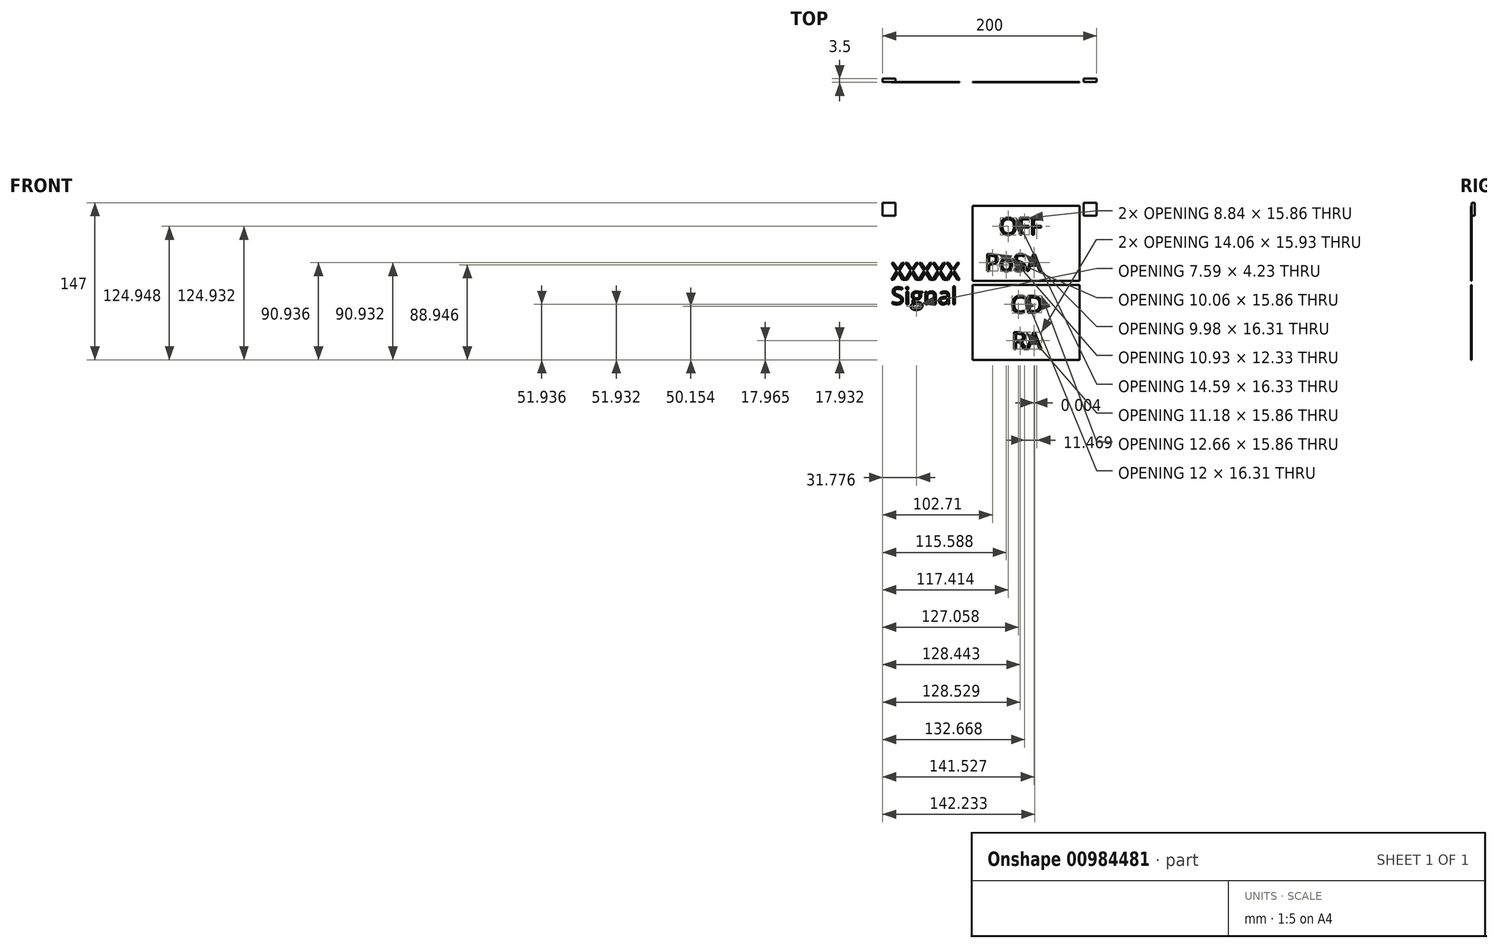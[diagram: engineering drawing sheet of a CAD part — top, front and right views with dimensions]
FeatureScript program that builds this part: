
annotation { "Feature Type Name" : "Feature", "Feature Type Description" : "" }
export const myFeature = defineFeature(function(context is Context, id is Id, definition is map)
    precondition{}
    {
        {
            var Q0;
            Q0=qCreatedBy(makeId("Front.planeOp"),FACE);
            var sketch = newSketch(context, id + "F0", { "sketchPlane" : qUnion([Q0])});
            skLineSegment(sketch, "E0.bottom", {"start": v(-152.92, 118.64) * mm, "end": v(47.08, 118.64) * mm});
            skLineSegment(sketch, "E0.top", {"start": v(-152.92, -31.36) * mm, "end": v(47.08, -31.36) * mm});
            skLineSegment(sketch, "E0.left", {"start": v(-152.92, 118.64) * mm, "end": v(-152.92, -31.36) * mm});
            skLineSegment(sketch, "E0.right", {"start": v(47.08, 118.64) * mm, "end": v(47.08, -31.36) * mm});
            skLineSegment(sketch, "E1.bottom", {"start": v(-140.92, 118.64) * mm, "end": v(-152.92, 118.64) * mm});
            skLineSegment(sketch, "E1.top", {"start": v(-140.92, 106.64) * mm, "end": v(-152.92, 106.64) * mm});
            skLineSegment(sketch, "E1.left", {"start": v(-140.92, 118.64) * mm, "end": v(-140.92, 106.64) * mm});
            skLineSegment(sketch, "E1.right", {"start": v(-152.92, 118.64) * mm, "end": v(-152.92, 106.64) * mm});
            skLineSegment(sketch, "E2.bottom", {"start": v(47.08, 106.64) * mm, "end": v(35.08, 106.64) * mm});
            skLineSegment(sketch, "E2.top", {"start": v(47.08, 118.64) * mm, "end": v(35.08, 118.64) * mm});
            skLineSegment(sketch, "E2.left", {"start": v(47.08, 106.64) * mm, "end": v(47.08, 118.64) * mm});
            skLineSegment(sketch, "E2.right", {"start": v(35.08, 106.64) * mm, "end": v(35.08, 118.64) * mm});
            skLineSegment(sketch, "E3.bottom", {"start": v(47.08, -19.36) * mm, "end": v(35.08, -19.36) * mm});
            skLineSegment(sketch, "E3.top", {"start": v(47.08, -31.36) * mm, "end": v(35.08, -31.36) * mm});
            skLineSegment(sketch, "E3.left", {"start": v(47.08, -19.36) * mm, "end": v(47.08, -31.36) * mm});
            skLineSegment(sketch, "E3.right", {"start": v(35.08, -19.36) * mm, "end": v(35.08, -31.36) * mm});
            skLineSegment(sketch, "E4.bottom", {"start": v(-152.92, -19.36) * mm, "end": v(-140.92, -19.36) * mm});
            skLineSegment(sketch, "E4.top", {"start": v(-152.92, -31.36) * mm, "end": v(-140.92, -31.36) * mm});
            skLineSegment(sketch, "E4.left", {"start": v(-152.92, -19.36) * mm, "end": v(-152.92, -31.36) * mm});
            skLineSegment(sketch, "E4.right", {"start": v(-140.92, -19.36) * mm, "end": v(-140.92, -31.36) * mm});
            skCircle(sketch, "E5", {"center": v(13.08, 96.64) * mm, "radius": 11 * mm});
            skCircle(sketch, "E6", {"center": v(13.08, 62.64) * mm, "radius": 11 * mm});
            skCircle(sketch, "E7", {"center": v(13.08, 23.64) * mm, "radius": 11 * mm});
            skCircle(sketch, "E8", {"center": v(13.08, -10.36) * mm, "radius": 11 * mm});
            skSolve(sketch);
        }
        {
            var Q0;
            Q0=makeQuery(id+"F0.imprint","IMPRINT",FACE,{"disambiguationData":[TD([[makeQuery(id+"F0.imprint","IMPRINT",EDGE,{"derivedFrom":sQuery(id+"F0.wireOp",EDGE,"E0.bottom")}),-1.0]])]});
            extrude(context, id + "F1", {"entities" : qUnion([Q0]), "depth" : 3 * mm, "offsetDistance" : 25 * mm});
        }
        {
            var Q0;
            Q0=makeQuery(id+"F1.opExtrude","CAP_FACE",FACE,{"disambiguationData":[OSD([sQuery(id+"F0.wireOp",EDGE,"E0.bottom"),sQuery(id+"F0.wireOp",EDGE,"E0.top"),sQuery(id+"F0.wireOp",EDGE,"E0.left"),sQuery(id+"F0.wireOp",EDGE,"E0.right"),sQuery(id+"F0.wireOp",EDGE,"E1.top"),sQuery(id+"F0.wireOp",EDGE,"E1.left"),sQuery(id+"F0.wireOp",EDGE,"E2.bottom"),sQuery(id+"F0.wireOp",EDGE,"E2.right"),sQuery(id+"F0.wireOp",EDGE,"E3.bottom"),sQuery(id+"F0.wireOp",EDGE,"E3.right"),sQuery(id+"F0.wireOp",EDGE,"E4.bottom"),sQuery(id+"F0.wireOp",EDGE,"E4.right"),sQuery(id+"F0.wireOp",EDGE,"E5"),sQuery(id+"F0.wireOp",EDGE,"E6"),sQuery(id+"F0.wireOp",EDGE,"E7"),sQuery(id+"F0.wireOp",EDGE,"E8")])],"isStart":false});
            var sketch = newSketch(context, id + "F2", { "sketchPlane" : qUnion([Q0])});
            skText(sketch, "E9", { "text": "XXXXX", "fontName": "OpenSans-Regular.ttf"});
            skText(sketch, "E10", { "text": "Signal", "fontName": "OpenSans-Regular.ttf"});
            skText(sketch, "E11", { "text": "OFF", "fontName": "OpenSans-Regular.ttf"});
            skText(sketch, "E12", { "text": "PoSA", "fontName": "OpenSans-Regular.ttf"});
            skText(sketch, "E13", { "text": "CD", "fontName": "OpenSans-Regular.ttf"});
            skText(sketch, "E14", { "text": "RA", "fontName": "OpenSans-Regular.ttf"});
            skLineSegment(sketch, "E15.bottom", {"start": v(-68.92, 115.64) * mm, "end": v(31.08, 115.64) * mm});
            skLineSegment(sketch, "E15.top", {"start": v(-68.92, 45.64) * mm, "end": v(31.08, 45.64) * mm});
            skLineSegment(sketch, "E15.left", {"start": v(-68.92, 115.64) * mm, "end": v(-68.92, 45.64) * mm});
            skLineSegment(sketch, "E15.right", {"start": v(31.08, 115.64) * mm, "end": v(31.08, 45.64) * mm});
            skLineSegment(sketch, "E16.bottom", {"start": v(-68.92, 41.64) * mm, "end": v(31.08, 41.64) * mm});
            skLineSegment(sketch, "E16.top", {"start": v(-68.92, -28.36) * mm, "end": v(31.08, -28.36) * mm});
            skLineSegment(sketch, "E16.left", {"start": v(-68.92, 41.64) * mm, "end": v(-68.92, -28.36) * mm});
            skLineSegment(sketch, "E16.right", {"start": v(31.08, 41.64) * mm, "end": v(31.08, -28.36) * mm});
            const initialGuessF2  = {"E9": [-0.14492, 0.04664, 1, 0, 0.016], "E10": [-0.14492, 0.02364, 1, 0, 0.016], "E11": [-0.04416, 0.08864, 1, 0, 0.016], "E12": [-0.05742, 0.05464, 1, 0, 0.016], "E13": [-0.03322, 0.01564, 1, 0, 0.016], "E14": [-0.03216, -0.01836, 1, 0, 0.016]};
            skSetInitialGuess(sketch, initialGuessF2);
            skSolve(sketch);
        }
        {
            var Q0;
            Q0=makeQuery(id+"F2.imprint","IMPRINT",FACE,{"disambiguationData":[TD([[makeQuery(id+"F2.imprint","IMPRINT",EDGE,{"derivedFrom":sQuery(id+"F2.wireOp",EDGE,"E12.sketch_text.stroke-8")}),1.0]])]});
            var Q1;
            Q1=makeQuery(id+"F2.imprint","IMPRINT",FACE,{"disambiguationData":[TD([[makeQuery(id+"F2.imprint","IMPRINT",EDGE,{"derivedFrom":sQuery(id+"F2.wireOp",EDGE,"E12.sketch_text.stroke-65")}),1.0]])]});
            var Q2;
            Q2=makeQuery(id+"F2.imprint","IMPRINT",FACE,{"disambiguationData":[TD([[makeQuery(id+"F2.imprint","IMPRINT",EDGE,{"derivedFrom":sQuery(id+"F2.wireOp",EDGE,"E12.sketch_text.stroke-24")}),1.0]])]});
            var Q3;
            Q3=makeQuery(id+"F2.imprint","IMPRINT",FACE,{"disambiguationData":[TD([[makeQuery(id+"F2.imprint","IMPRINT",EDGE,{"derivedFrom":sQuery(id+"F2.wireOp",EDGE,"E11.sketch_text.stroke-8")}),1.0]])]});
            var Q4;
            Q4=makeQuery(id+"F2.imprint","IMPRINT",FACE,{"disambiguationData":[TD([[makeQuery(id+"F2.imprint","IMPRINT",EDGE,{"derivedFrom":sQuery(id+"F2.wireOp",EDGE,"E13.sketch_text.stroke-22")}),1.0]])]});
            var Q5;
            Q5=makeQuery(id+"F2.imprint","IMPRINT",FACE,{"disambiguationData":[TD([[makeQuery(id+"F2.imprint","IMPRINT",EDGE,{"derivedFrom":sQuery(id+"F2.wireOp",EDGE,"E14.sketch_text.stroke-26")}),1.0]])]});
            var Q6;
            Q6=makeQuery(id+"F2.imprint","IMPRINT",FACE,{"disambiguationData":[TD([[makeQuery(id+"F2.imprint","IMPRINT",EDGE,{"derivedFrom":sQuery(id+"F2.wireOp",EDGE,"E14.sketch_text.stroke-11")}),1.0]])]});
            var Q7;
            Q7=makeQuery(id+"F2.imprint","IMPRINT",FACE,{"disambiguationData":[TD([[makeQuery(id+"F2.imprint","IMPRINT",EDGE,{"derivedFrom":sQuery(id+"F2.wireOp",EDGE,"E9.sketch_text.stroke-0")}),-1.0]])]});
            var Q8;
            Q8=makeQuery(id+"F2.imprint","IMPRINT",FACE,{"disambiguationData":[TD([[makeQuery(id+"F2.imprint","IMPRINT",EDGE,{"derivedFrom":sQuery(id+"F2.wireOp",EDGE,"E9.sketch_text.stroke-12")}),-1.0]])]});
            var Q9;
            Q9=makeQuery(id+"F2.imprint","IMPRINT",FACE,{"disambiguationData":[TD([[makeQuery(id+"F2.imprint","IMPRINT",EDGE,{"derivedFrom":sQuery(id+"F2.wireOp",EDGE,"E9.sketch_text.stroke-24")}),-1.0]])]});
            var Q10;
            Q10=makeQuery(id+"F2.imprint","IMPRINT",FACE,{"disambiguationData":[TD([[makeQuery(id+"F2.imprint","IMPRINT",EDGE,{"derivedFrom":sQuery(id+"F2.wireOp",EDGE,"E9.sketch_text.stroke-36")}),-1.0]])]});
            var Q11;
            Q11=makeQuery(id+"F2.imprint","IMPRINT",FACE,{"disambiguationData":[TD([[makeQuery(id+"F2.imprint","IMPRINT",EDGE,{"derivedFrom":sQuery(id+"F2.wireOp",EDGE,"E9.sketch_text.stroke-48")}),-1.0]])]});
            var Q12;
            Q12=makeQuery(id+"F2.imprint","IMPRINT",FACE,{"disambiguationData":[TD([[makeQuery(id+"F2.imprint","IMPRINT",EDGE,{"derivedFrom":sQuery(id+"F2.wireOp",EDGE,"E10.sketch_text.stroke-0")}),-1.0]])]});
            var Q13;
            Q13=makeQuery(id+"F2.imprint","IMPRINT",FACE,{"disambiguationData":[TD([[makeQuery(id+"F2.imprint","IMPRINT",EDGE,{"derivedFrom":sQuery(id+"F2.wireOp",EDGE,"E10.sketch_text.stroke-25")}),-1.0]])]});
            var Q14;
            Q14=makeQuery(id+"F2.imprint","IMPRINT",FACE,{"disambiguationData":[TD([[makeQuery(id+"F2.imprint","IMPRINT",EDGE,{"derivedFrom":sQuery(id+"F2.wireOp",EDGE,"E10.sketch_text.stroke-29")}),-1.0]])]});
            var Q15;
            Q15=makeQuery(id+"F2.imprint","IMPRINT",FACE,{"disambiguationData":[TD([[makeQuery(id+"F2.imprint","IMPRINT",EDGE,{"derivedFrom":sQuery(id+"F2.wireOp",EDGE,"E10.sketch_text.stroke-81")}),-1.0]])]});
            var Q16;
            Q16=makeQuery(id+"F2.imprint","IMPRINT",FACE,{"disambiguationData":[TD([[makeQuery(id+"F2.imprint","IMPRINT",EDGE,{"derivedFrom":sQuery(id+"F2.wireOp",EDGE,"E10.sketch_text.stroke-125")}),-1.0]])]});
            var Q17;
            Q17=makeQuery(id+"F2.imprint","IMPRINT",FACE,{"disambiguationData":[TD([[makeQuery(id+"F2.imprint","IMPRINT",EDGE,{"derivedFrom":sQuery(id+"F2.wireOp",EDGE,"E10.sketch_text.stroke-98")}),-1.0]])]});
            var Q18;
            Q18=makeQuery(id+"F2.imprint","IMPRINT",FACE,{"disambiguationData":[TD([[makeQuery(id+"F2.imprint","IMPRINT",EDGE,{"derivedFrom":sQuery(id+"F2.wireOp",EDGE,"E10.sketch_text.stroke-37")}),-1.0]])]});
            var Q19;
            Q19=makeQuery(id+"F2.imprint","IMPRINT",FACE,{"disambiguationData":[TD([[makeQuery(id+"F2.imprint","IMPRINT",EDGE,{"derivedFrom":sQuery(id+"F2.wireOp",EDGE,"E13.sketch_text.stroke-0")}),1.0]])]});
            var Q20;
            Q20=makeQuery(id+"F2.imprint","IMPRINT",FACE,{"disambiguationData":[TD([[makeQuery(id+"F2.imprint","IMPRINT",EDGE,{"derivedFrom":sQuery(id+"F2.wireOp",EDGE,"E11.sketch_text.stroke-0")}),1.0]])]});
            extrude(context, id + "F3", {"entities" : qUnion([Q0, Q1, Q2, Q3, Q4, Q5, Q6, Q7, Q8, Q9, Q10, Q11, Q12, Q13, Q14, Q15, Q16, Q17, Q18, Q19, Q20]), "operationType" : NewBodyOperationType.ADD, "depth" : .5 * mm, "offsetDistance" : 25 * mm});
        }
    });
